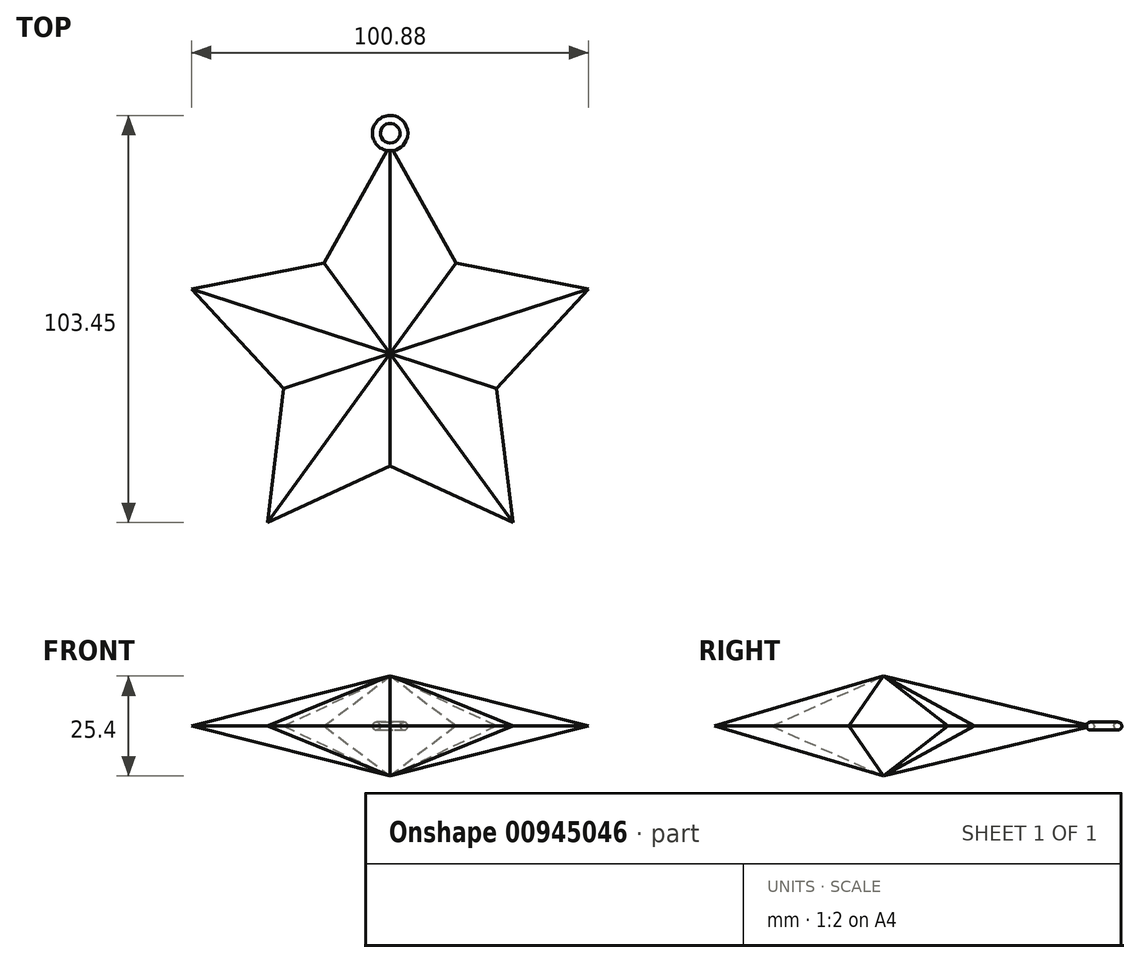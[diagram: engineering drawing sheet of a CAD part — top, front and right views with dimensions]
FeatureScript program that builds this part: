
annotation { "Feature Type Name" : "Feature", "Feature Type Description" : "" }
export const myFeature = defineFeature(function(context is Context, id is Id, definition is map)
    precondition{}
    {
        {
            var Q0;
            Q0=qCreatedBy(makeId("Top.planeOp"),FACE);
            var sketch = newSketch(context, id + "F0", { "sketchPlane" : qUnion([Q0])});
            skLineSegment(sketch, "E0", {"start": v(0, 53.04) * mm, "end": v(-16.73, 23.03) * mm});
            skLineSegment(sketch, "E1.MirrorCS", {"start": v(0, 53.04) * mm, "end": v(16.73, 23.03) * mm});
            skLineSegment(sketch, "E2.1.0", {"start": v(-50.44, 16.39) * mm, "end": v(-27.07, -8.8) * mm});
            skLineSegment(sketch, "E2.1.1", {"start": v(-50.44, 16.39) * mm, "end": v(-16.73, 23.03) * mm});
            skLineSegment(sketch, "E2.2.0", {"start": v(-31.17, -42.9) * mm, "end": v(0, -28.47) * mm});
            skLineSegment(sketch, "E2.2.1", {"start": v(-31.17, -42.9) * mm, "end": v(-27.07, -8.8) * mm});
            skLineSegment(sketch, "E2.3.0", {"start": v(31.17, -42.9) * mm, "end": v(27.07, -8.8) * mm});
            skLineSegment(sketch, "E2.3.1", {"start": v(31.17, -42.9) * mm, "end": v(0, -28.47) * mm});
            skLineSegment(sketch, "E2.4.0", {"start": v(50.44, 16.39) * mm, "end": v(16.73, 23.03) * mm});
            skLineSegment(sketch, "E2.4.1", {"start": v(50.44, 16.39) * mm, "end": v(27.07, -8.8) * mm});
            skPoint(sketch, "E2.center", {"position": v(0, 0) * mm});
            skPoint(sketch, "E3.orphan", {"position": v(-23.93, -17.38) * mm});
            skPoint(sketch, "E4.orphan", {"position": v(-9.14, -28.13) * mm});
            skPoint(sketch, "E5.orphan", {"position": v(23.93, 17.38) * mm});
            skPoint(sketch, "E6.orphan", {"position": v(29.57, 0) * mm});
            skPoint(sketch, "E7.orphan", {"position": v(-23.93, 17.38) * mm});
            skPoint(sketch, "E8.trimOffspring.end.orphan", {"position": v(-29.57, 0) * mm});
            skSolve(sketch);
        }
        {
            var Q0;
            Q0=qCreatedBy(makeId("Top.planeOp"),FACE);
            cPlane(context, id + "F1", {"entities" : qUnion([Q0]), "cplaneType" : CPlaneType.OFFSET, "offset" : 12.7 * mm, "width" : 152.4 * mm, "height" : 152.4 * mm});
        }
        {
            var Q0;
            Q0=qCreatedBy(id+"F1.planeOp",FACE);
            var sketch = newSketch(context, id + "F2", { "sketchPlane" : qUnion([Q0])});
            skPoint(sketch, "E9", {"position": v(0, 0) * mm});
            skSolve(sketch);
        }
        {
            var Q0;
            Q0 = qSketchRegion(id + "F0", true);
            var Q1;
            Q1=sQuery(id+"F2.wireOp",VERTEX,"E9");
            loft(context, id + "F3", {"sheetProfilesArray" : [{ "sheetProfileEntities" : qUnion([Q0]) }, { "sheetProfileEntities" : qUnion([Q1]) }]});
        }
        {
            var Q0;
            Q0=makeQuery(id+"F3.opLoft","SWEPT_BODY",BODY,{"disambiguationData":[OSD([makeQuery(id+"F0.imprint","IMPRINT",FACE,{"disambiguationData":[TD([[makeQuery(id+"F0.imprint","IMPRINT",EDGE,{"derivedFrom":sQuery(id+"F0.wireOp",EDGE,"E0")}),1.0]])]}),sQuery(id+"F2.wireOp",VERTEX,"E9")])]});
            var Q1;
            Q1=qCreatedBy(makeId("Top.planeOp"),FACE);
            mirror(context, id + "F4", {"operationType" : NewBodyOperationType.ADD, "entities" : qUnion([Q0]), "mirrorPlane" : qUnion([Q1])});
        }
        {
            var Q0;
            Q0=qCreatedBy(makeId("Top.planeOp"),FACE);
            var sketch = newSketch(context, id + "F5", { "sketchPlane" : qUnion([Q0])});
            skCircle(sketch, "E10", {"center": v(0, 56.04) * mm, "radius": 3.75 * mm});
            skSolve(sketch);
        }
        {
            var Q0;
            Q0=qCreatedBy(makeId("Right.planeOp"),FACE);
            var sketch = newSketch(context, id + "F6", { "sketchPlane" : qUnion([Q0])});
            skCircle(sketch, "E11", {"center": v(59.54, 0) * mm, "radius": 1 * mm});
            skSolve(sketch);
        }
        {
            var Q0;
            Q0=makeQuery(id+"F6.imprint","IMPRINT",FACE,{"disambiguationData":[TD([[makeQuery(id+"F6.imprint","IMPRINT",EDGE,{"derivedFrom":sQuery(id+"F6.wireOp",EDGE,"E11")}),1.0]])]});
            var Q1;
            Q1=sQuery(id+"F5.wireOp",EDGE,"E10");
            sweep(context, id + "F7", {"operationType" : NewBodyOperationType.ADD, "profiles" : qUnion([Q0]), "path" : qUnion([Q1])});
        }
    });
